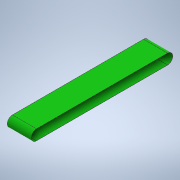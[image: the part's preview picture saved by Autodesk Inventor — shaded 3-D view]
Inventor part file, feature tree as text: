
AUTODESK INVENTOR PART (.ipt)
format: ipt  version: 2020 (Build 240168000, 168)  size: 117,248 bytes
history: native  units: in
note: dims shown in document units (in); Inventor stores cm internally (conversion verified against a paired STEP export)
features: extrude x2, sketch x2
ambient origin geometry x8: Origin, YZ Plane, XZ Plane, XY Plane, X Axis, Y Axis, Z Axis, Center Point
bodies: Solid1 (feature_tree)
feature tree (4):
  extrude  "Extrusion1"  Depth=1.5354in
  extrude  "Extrusion2"  Depth=3.5433in TaperAngle=0.0deg
  sketch  "Sketch1"  dims[d0=1.5354in d1=1.5354in]
  sketch  "Sketch2"  dims[d2=19.2913in d3=3.5433in d4=0.0in d5=1.4961in d6=1.4961in d7=0.0in d8=0.0in]
